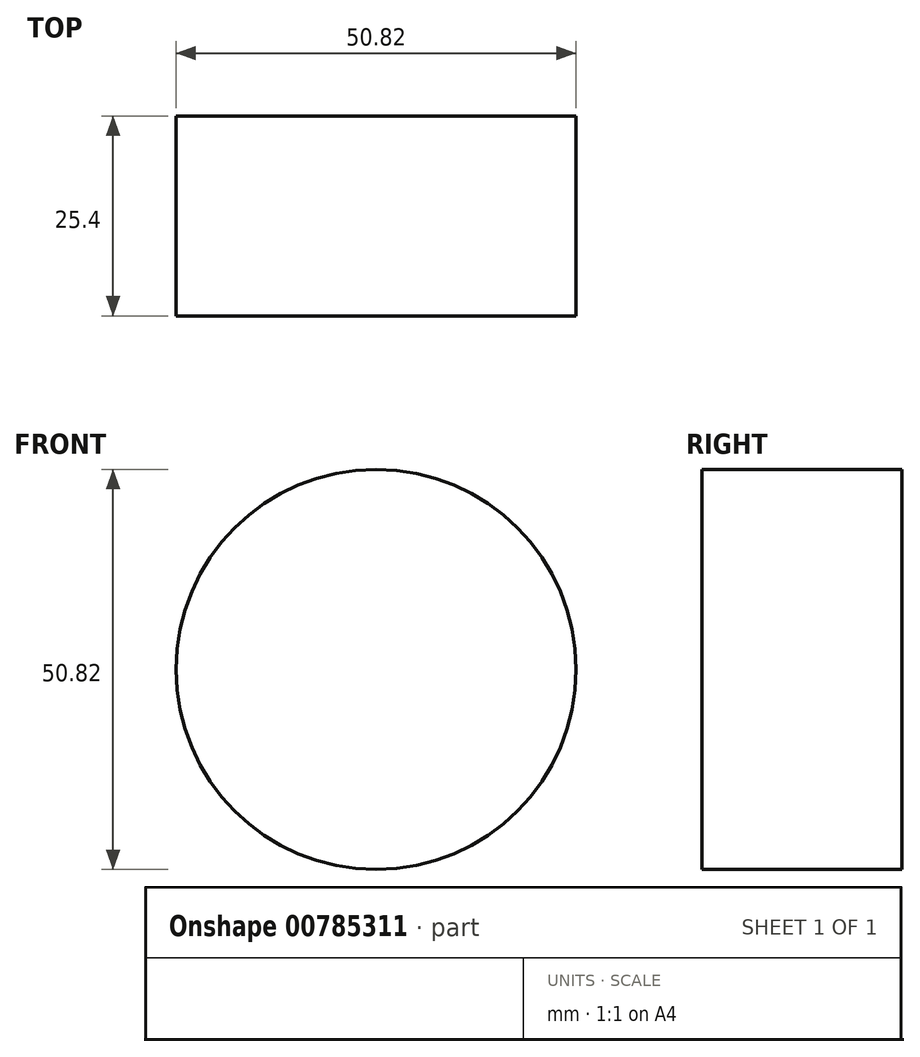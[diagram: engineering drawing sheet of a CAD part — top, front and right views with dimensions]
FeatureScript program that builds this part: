
annotation { "Feature Type Name" : "Feature", "Feature Type Description" : "" }
export const myFeature = defineFeature(function(context is Context, id is Id, definition is map)
    precondition{}
    {
        {
            var Q0;
            Q0=qCreatedBy(makeId("Front.planeOp"),FACE);
            var sketch = newSketch(context, id + "F0", { "sketchPlane" : qUnion([Q0])});
            skCircle(sketch, "E0", {"center": v(-72.63, 34.63) * mm, "radius": 25.4 * mm});
            skSolve(sketch);
        }
        {
            var Q0;
            Q0=makeQuery(id+"F0.imprint","IMPRINT",FACE,{"disambiguationData":[TD([[makeQuery(id+"F0.imprint","IMPRINT",EDGE,{"derivedFrom":sQuery(id+"F0.wireOp",EDGE,"E0")}),1.0]])]});
            extrude(context, id + "F1", {"entities" : qUnion([Q0]), "depth" : 25.4 * mm, "offsetDistance" : 25.4 * mm});
        }
    });
